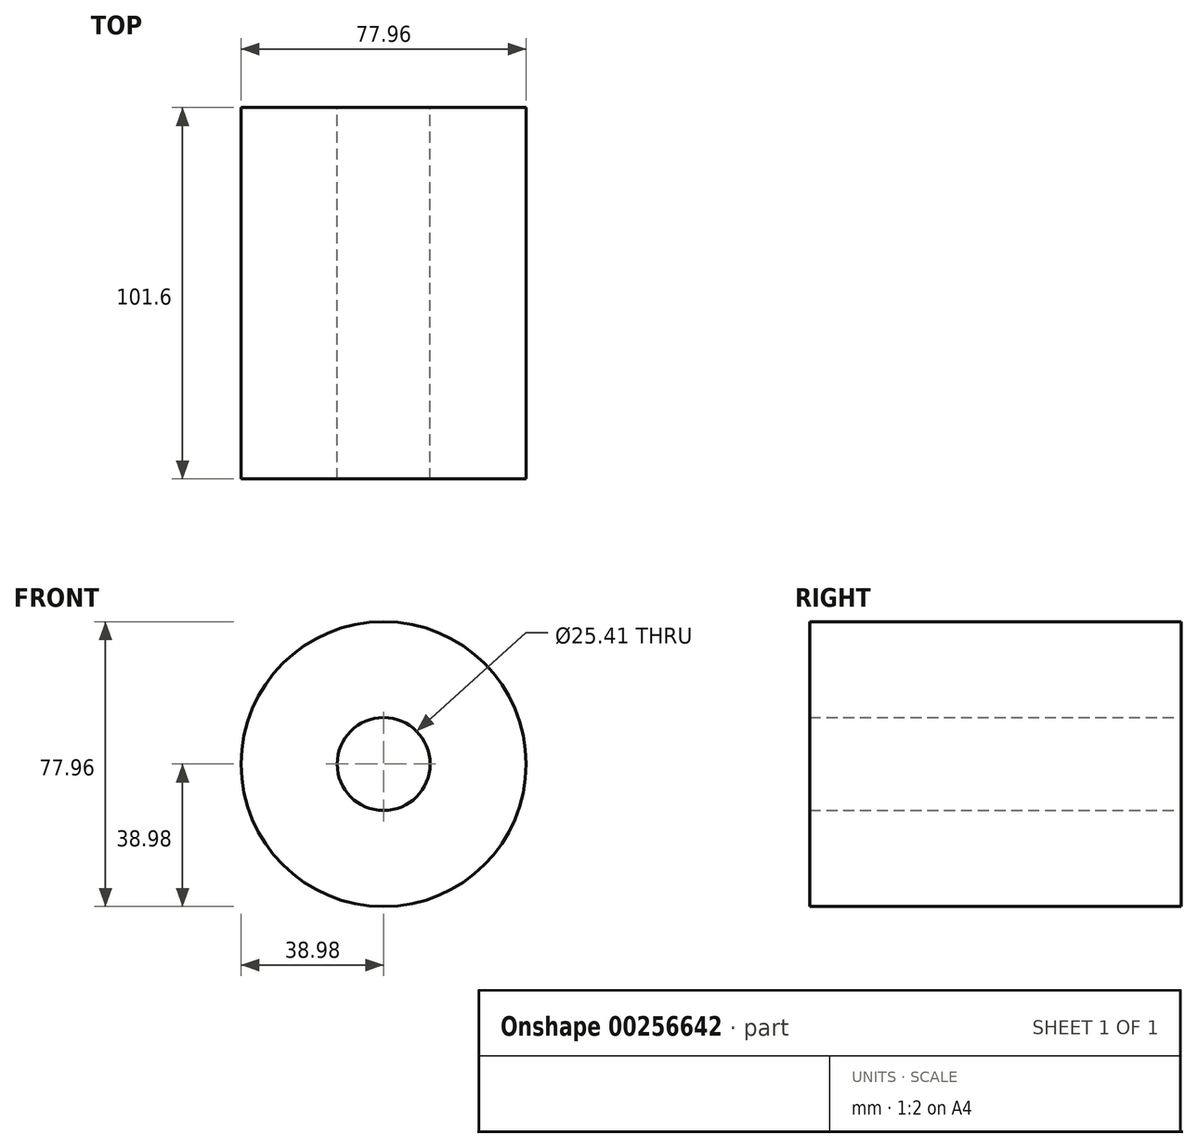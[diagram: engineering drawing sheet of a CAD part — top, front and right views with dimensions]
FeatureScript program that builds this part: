
annotation { "Feature Type Name" : "Feature", "Feature Type Description" : "" }
export const myFeature = defineFeature(function(context is Context, id is Id, definition is map)
    precondition{}
    {
        {
            var Q0;
            Q0=qCreatedBy(makeId("Front.planeOp"),FACE);
            var sketch = newSketch(context, id + "F0", { "sketchPlane" : qUnion([Q0])});
            skCircle(sketch, "E0", {"center": v(0, 0) * mm, "radius": 38.98 * mm});
            skCircle(sketch, "E1", {"center": v(0, 0) * mm, "radius": 12.7 * mm});
            skSolve(sketch);
        }
        {
            var Q0;
            Q0 = qSketchRegion(id + "F0", true);
            extrude(context, id + "F1", {"entities" : qUnion([Q0]), "depth" : 101.6 * mm});
        }
    });
